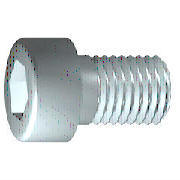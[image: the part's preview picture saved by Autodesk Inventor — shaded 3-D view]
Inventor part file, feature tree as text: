
AUTODESK INVENTOR PART (.ipt)
format: ipt  version: 2023.3 (Build 273359000, 359)  size: 187,392 bytes
history: native  units: mm (DEFAULTED — no unit token found)
features: sketch x2, other x1, extrude x1, plane x1, fillet x1
ambient origin geometry x7: Origin, YZ Plane, XY Plane, X Axis, Y Axis, Z Axis, Center Point
bodies: Solid1 (feature_tree)
feature tree (6):
  other  "Körper"
  extrude  "Loch"  Depth=2.5mm
  plane  "Work Plane1"
  fillet  "Fillet2"  Radius=2.5mm
  sketch  "Skizze1"  dims[d1=14.875mm d2=0.276153mm d3=2.5mm]
  sketch  "Skizze2"  dims[d4=1.1mm d5=60.0deg d6=2.5mm d7=2.5mm d8=2.309401mm d9=4.5mm d10=90.0deg d11=10.0mm d12=0.0mm d13=14.875mm d14=0.0mm d15=0.276052mm d16=0.276053mm d17=0.25mm d19=0.0mm d26=16.0mm d27=45.0deg d28=0.0mm d29=0.0mm d30=0.1mm]
